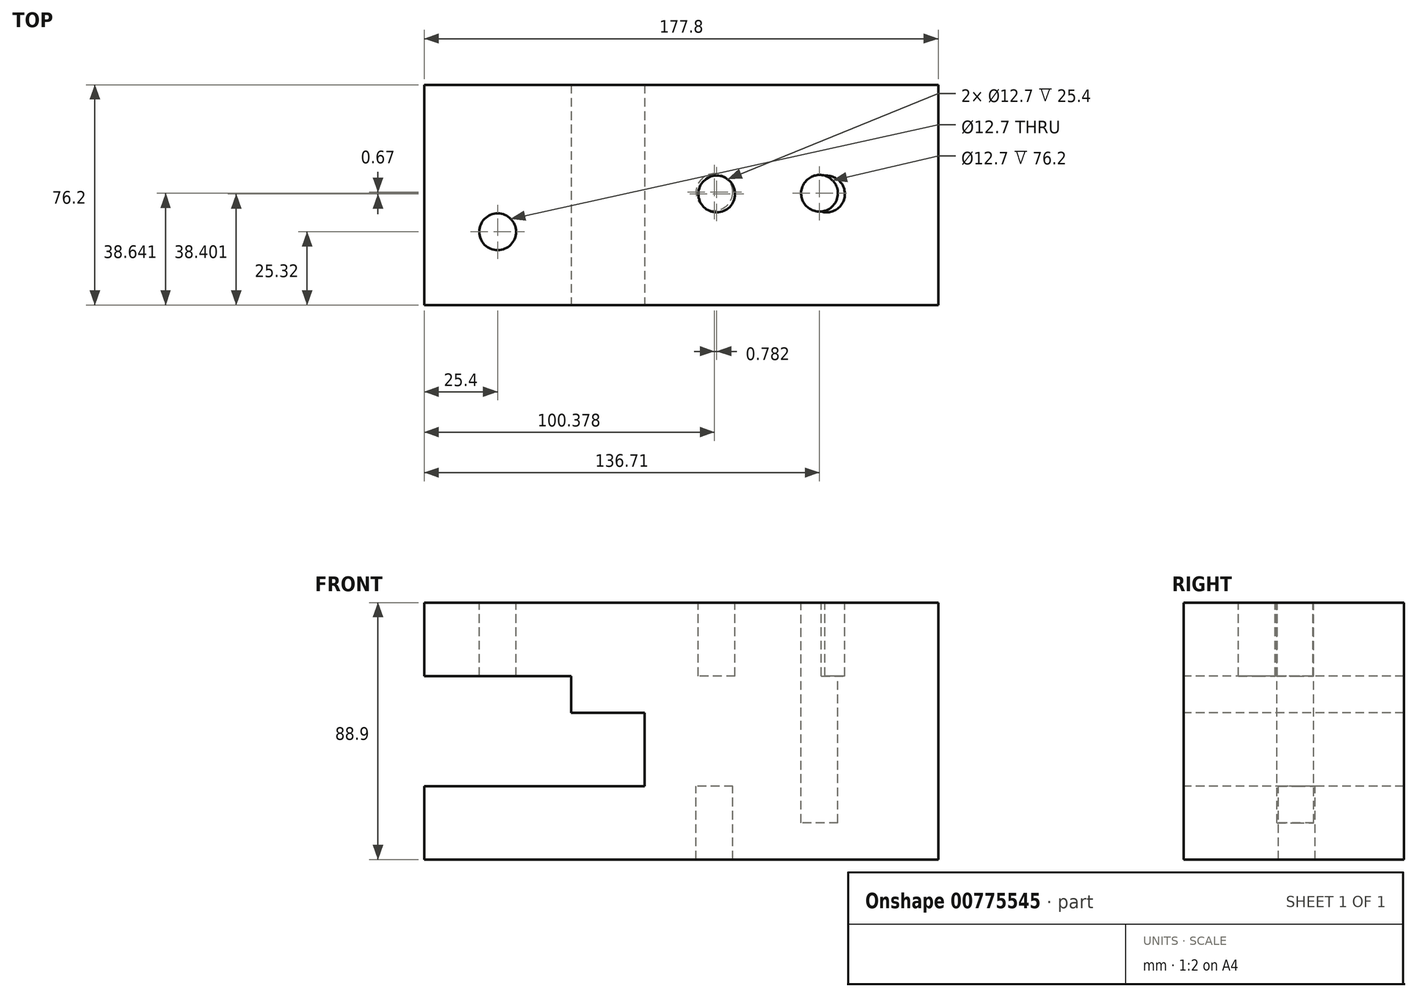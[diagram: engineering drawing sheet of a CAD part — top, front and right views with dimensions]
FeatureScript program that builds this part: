
annotation { "Feature Type Name" : "Feature", "Feature Type Description" : "" }
export const myFeature = defineFeature(function(context is Context, id is Id, definition is map)
    precondition{}
    {
        {
            var Q0;
            Q0=qCreatedBy(makeId("Front.planeOp"),FACE);
            var sketch = newSketch(context, id + "F0", { "sketchPlane" : qUnion([Q0])});
            skLineSegment(sketch, "E0.bottom", {"start": v(0, 0) * mm, "end": v(177.8, 0) * mm});
            skLineSegment(sketch, "E0.top", {"start": v(0, -88.9) * mm, "end": v(177.8, -88.9) * mm});
            skLineSegment(sketch, "E0.left", {"start": v(0, 0) * mm, "end": v(0, -88.9) * mm});
            skLineSegment(sketch, "E0.right", {"start": v(177.8, 0) * mm, "end": v(177.8, -88.9) * mm});
            skSolve(sketch);
        }
        {
            var Q0;
            Q0=makeQuery(id+"F0.imprint","IMPRINT",FACE,{"disambiguationData":[TD([[makeQuery(id+"F0.imprint","IMPRINT",EDGE,{"derivedFrom":sQuery(id+"F0.wireOp",EDGE,"E0.bottom")}),-1.0]])]});
            extrude(context, id + "F1", {"entities" : qUnion([Q0]), "depth" : 76.2 * mm, "offsetDistance" : 25.4 * mm});
        }
        {
            var Q0;
            Q0=makeQuery(id+"F1.opExtrude","CAP_FACE",FACE,{"disambiguationData":[OSD([sQuery(id+"F0.wireOp",EDGE,"E0.bottom"),sQuery(id+"F0.wireOp",EDGE,"E0.top"),sQuery(id+"F0.wireOp",EDGE,"E0.left"),sQuery(id+"F0.wireOp",EDGE,"E0.right")])],"isStart":false});
            var sketch = newSketch(context, id + "F2", { "sketchPlane" : qUnion([Q0])});
            skLineSegment(sketch, "E1", {"start": v(0, -88.9) * mm, "end": v(0, -63.5) * mm});
            skLineSegment(sketch, "E2", {"start": v(0, -63.5) * mm, "end": v(177.8, -63.5) * mm});
            skLineSegment(sketch, "E3", {"start": v(177.8, -63.5) * mm, "end": v(177.8, -88.9) * mm});
            skLineSegment(sketch, "E4", {"start": v(177.8, -88.9) * mm, "end": v(0, -88.9) * mm});
            skLineSegment(sketch, "E5", {"start": v(0, 0) * mm, "end": v(50.8, 0) * mm});
            skLineSegment(sketch, "E6", {"start": v(50.8, 0) * mm, "end": v(50.8, -38.1) * mm});
            skLineSegment(sketch, "E7", {"start": v(50.8, -38.1) * mm, "end": v(76.2, -38.1) * mm});
            skLineSegment(sketch, "E8", {"start": v(76.2, -38.1) * mm, "end": v(76.2, -63.5) * mm});
            skLineSegment(sketch, "E9", {"start": v(76.2, -63.5) * mm, "end": v(0, -63.5) * mm});
            skLineSegment(sketch, "E10", {"start": v(0, 0) * mm, "end": v(0, -25.4) * mm});
            skLineSegment(sketch, "E11", {"start": v(0, -25.4) * mm, "end": v(50.8, -25.4) * mm});
            skLineSegment(sketch, "E12", {"start": v(0, -25.4) * mm, "end": v(0, -63.5) * mm});
            skSolve(sketch);
        }
        {
            var Q0;
            {var subQ0=sQuery(id+"F2.wireOp",EDGE,"E5");Q0=makeQuery(id+"F2.imprint","IMPRINT",FACE,{"disambiguationData":[TD([[makeQuery(id+"F2.imprint","IMPRINT",EDGE,{"derivedFrom":subQ0}),-1.0]])]});}
            var Q1;
            Q1=makeQuery(id+"F2.imprint","IMPRINT",FACE,{"disambiguationData":[TD([[makeQuery(id+"F2.imprint","IMPRINT",EDGE,{"derivedFrom":sQuery(id+"F2.wireOp",EDGE,"E1")}),1.0]])]});
            var Q2;
            {var subQ0=sQuery(id+"F2.wireOp",EDGE,"E7");Q2=makeQuery(id+"F2.imprint","IMPRINT",FACE,{"disambiguationData":[TD([[makeQuery(id+"F2.imprint","IMPRINT",EDGE,{"derivedFrom":subQ0}),-1.0]])]});}
            extrude(context, id + "F3", {"entities" : qUnion([Q0, Q1, Q2]), "operationType" : NewBodyOperationType.ADD, "oppositeDirection" : true, "depth" : 76.2 * mm, "offsetDistance" : 25.4 * mm});
        }
        {
            var Q0;
            {var subQ0=sQuery(id+"F2.wireOp",EDGE,"E5");Q0=makeQuery(id+"F2.imprint","IMPRINT",FACE,{"disambiguationData":[TD([[makeQuery(id+"F2.imprint","IMPRINT",EDGE,{"derivedFrom":subQ0}),-1.0]])]});}
            var Q1;
            {var subQ0=sQuery(id+"F2.wireOp",EDGE,"E7");Q1=makeQuery(id+"F2.imprint","IMPRINT",FACE,{"disambiguationData":[TD([[makeQuery(id+"F2.imprint","IMPRINT",EDGE,{"derivedFrom":subQ0}),-1.0]])]});}
            var Q2;
            Q2=makeQuery(id+"F2.imprint","IMPRINT",FACE,{"disambiguationData":[TD([[makeQuery(id+"F2.imprint","IMPRINT",EDGE,{"derivedFrom":sQuery(id+"F2.wireOp",EDGE,"E1")}),1.0]])]});
            extrude(context, id + "F4", {"entities" : qUnion([Q0, Q1, Q2]), "operationType" : NewBodyOperationType.ADD, "oppositeDirection" : true, "depth" : 76.2 * mm, "offsetDistance" : 25.4 * mm});
        }
        {
            var Q0;
            {var subQ5=sQuery(id+"F2.wireOp",EDGE,"E2");Q0=makeQuery(id+"F2.imprint","IMPRINT",FACE,{"disambiguationData":[TD([[makeQuery(id+"F2.imprint","IMPRINT",EDGE,{"derivedFrom":subQ5}),1.0]])]});}
            extrude(context, id + "F5", {"entities" : qUnion([Q0]), "operationType" : NewBodyOperationType.REMOVE, "oppositeDirection" : true, "depth" : 76.2 * mm, "offsetDistance" : 25.4 * mm});
        }
        {
            var Q0;
            {var subQ0=sQuery(id+"F2.wireOp",EDGE,"E7");Q0=makeQuery(id+"F2.imprint","IMPRINT",FACE,{"disambiguationData":[TD([[makeQuery(id+"F2.imprint","IMPRINT",EDGE,{"derivedFrom":subQ0}),-1.0]])]});}
            extrude(context, id + "F6", {"entities" : qUnion([Q0]), "operationType" : NewBodyOperationType.ADD, "oppositeDirection" : true, "depth" : 50.8 * mm, "offsetDistance" : 25.4 * mm});
        }
        {
            var Q0;
            {var subQ0=sQuery(id+"F2.wireOp",EDGE,"E7");Q0=makeQuery(id+"F2.imprint","IMPRINT",FACE,{"disambiguationData":[TD([[makeQuery(id+"F2.imprint","IMPRINT",EDGE,{"derivedFrom":subQ0}),-1.0]])]});}
            extrude(context, id + "F7", {"entities" : qUnion([Q0]), "operationType" : NewBodyOperationType.REMOVE, "oppositeDirection" : true, "depth" : 50.8 * mm, "offsetDistance" : 25.4 * mm});
        }
        {
            var Q0;
            Q0=qCreatedBy(makeId("Top.planeOp"),FACE);
            var sketch = newSketch(context, id + "F8", { "sketchPlane" : qUnion([Q0])});
            skCircle(sketch, "E13", {"center": v(25.4, -50.08) * mm, "radius": 6.35 * mm});
            skSolve(sketch);
        }
        {
            var Q0;
            Q0 = qSketchRegion(id + "F8", true);
            extrude(context, id + "F9", {"entities" : qUnion([Q0]), "operationType" : NewBodyOperationType.ADD, "oppositeDirection" : true, "depth" : 25.4 * mm, "offsetDistance" : 25.4 * mm});
        }
        {
            var Q0;
            Q0=qCreatedBy(makeId("Top.planeOp"),FACE);
            var sketch = newSketch(context, id + "F10", { "sketchPlane" : qUnion([Q0])});
            skLineSegment(sketch, "E14", {"start": v(0, -76.28) * mm, "end": v(0, -50.88) * mm});
            skLineSegment(sketch, "E15", {"start": v(0, -50.88) * mm, "end": v(25.4, -50.88) * mm});
            skCircle(sketch, "E16", {"center": v(25.4, -50.88) * mm, "radius": 6.35 * mm});
            skSolve(sketch);
        }
        {
            var Q0;
            Q0=makeQuery(id+"F10.imprint","IMPRINT",FACE,{"disambiguationData":[TD([[makeQuery(id+"F10.imprint","IMPRINT",EDGE,{"derivedFrom":sQuery(id+"F10.wireOp",EDGE,"E16")}),1.0]])]});
            extrude(context, id + "F11", {"entities" : qUnion([Q0]), "operationType" : NewBodyOperationType.REMOVE, "oppositeDirection" : true, "depth" : 25.4 * mm, "offsetDistance" : 25.4 * mm});
        }
        {
            var Q0;
            Q0=makeQuery(id+"F10.imprint","IMPRINT",FACE,{"disambiguationData":[TD([[makeQuery(id+"F10.imprint","IMPRINT",EDGE,{"derivedFrom":sQuery(id+"F10.wireOp",EDGE,"E16")}),1.0]])]});
            extrude(context, id + "F12", {"entities" : qUnion([Q0]), "operationType" : NewBodyOperationType.REMOVE, "oppositeDirection" : true, "depth" : 25.4 * mm, "offsetDistance" : 25.4 * mm});
        }
        {
            var Q0;
            Q0=qCreatedBy(makeId("Top.planeOp"),FACE);
            var sketch = newSketch(context, id + "F13", { "sketchPlane" : qUnion([Q0])});
            skLineSegment(sketch, "E17", {"start": v(178.87, -75.25) * mm, "end": v(178.87, -37.15) * mm});
            skLineSegment(sketch, "E18", {"start": v(177.07, 0) * mm, "end": v(138.97, 0) * mm});
            skCircle(sketch, "E19", {"center": v(139.14, -37.8) * mm, "radius": 6.35 * mm});
            skLineSegment(sketch, "E20", {"start": v(138.97, 0) * mm, "end": v(100.87, 0) * mm});
            skCircle(sketch, "E21", {"center": v(101.16, -37.8) * mm, "radius": 6.35 * mm});
            skSolve(sketch);
        }
        {
            var Q0;
            Q0 = qSketchRegion(id + "F13", true);
            extrude(context, id + "F14", {"entities" : qUnion([Q0]), "operationType" : NewBodyOperationType.REMOVE, "oppositeDirection" : true, "depth" : 25.4 * mm, "offsetDistance" : 25.4 * mm});
        }
        {
            var Q0;
            Q0=makeQuery(id+"F7.boolean.opBoolean","MERGE",FACE,{"derivedFrom":[makeQuery(id+"F5.boolean.opBoolean","COPY",FACE,{"derivedFrom":makeQuery(id+"F5.opExtrude","SWEPT_FACE",FACE,{"disambiguationData":[OSD([sQuery(id+"F2.wireOp",EDGE,"E2")])]})}),makeQuery(id+"F7.opExtrude","SWEPT_FACE",FACE,{"disambiguationData":[OSD([sQuery(id+"F2.wireOp",EDGE,"E9")])]})]});
            var sketch = newSketch(context, id + "F15", { "sketchPlane" : qUnion([Q0])});
            skCircle(sketch, "E22", {"center": v(141.32, -37.92) * mm, "radius": 6.35 * mm});
            skCircle(sketch, "E23", {"center": v(100.38, -37.13) * mm, "radius": 6.35 * mm});
            skSolve(sketch);
        }
        {
            var Q0;
            Q0=makeQuery(id+"F15.imprint","IMPRINT",FACE,{"disambiguationData":[TD([[makeQuery(id+"F15.imprint","IMPRINT",EDGE,{"derivedFrom":sQuery(id+"F15.wireOp",EDGE,"E23")}),1.0]])]});
            extrude(context, id + "F16", {"entities" : qUnion([Q0]), "operationType" : NewBodyOperationType.REMOVE, "oppositeDirection" : true, "depth" : 50.8 * mm, "offsetDistance" : 25.4 * mm});
        }
        {
            var Q0;
            Q0=qCreatedBy(makeId("Top.planeOp"),FACE);
            var sketch = newSketch(context, id + "F17", { "sketchPlane" : qUnion([Q0])});
            skCircle(sketch, "E24", {"center": v(136.71, -37.56) * mm, "radius": 6.35 * mm});
            skSolve(sketch);
        }
        {
            var Q0;
            Q0=makeQuery(id+"F17.imprint","IMPRINT",FACE,{"disambiguationData":[TD([[makeQuery(id+"F17.imprint","IMPRINT",EDGE,{"derivedFrom":sQuery(id+"F17.wireOp",EDGE,"E24")}),1.0]])]});
            extrude(context, id + "F18", {"entities" : qUnion([Q0]), "operationType" : NewBodyOperationType.REMOVE, "oppositeDirection" : true, "depth" : 76.2 * mm, "offsetDistance" : 25.4 * mm});
        }
    });
